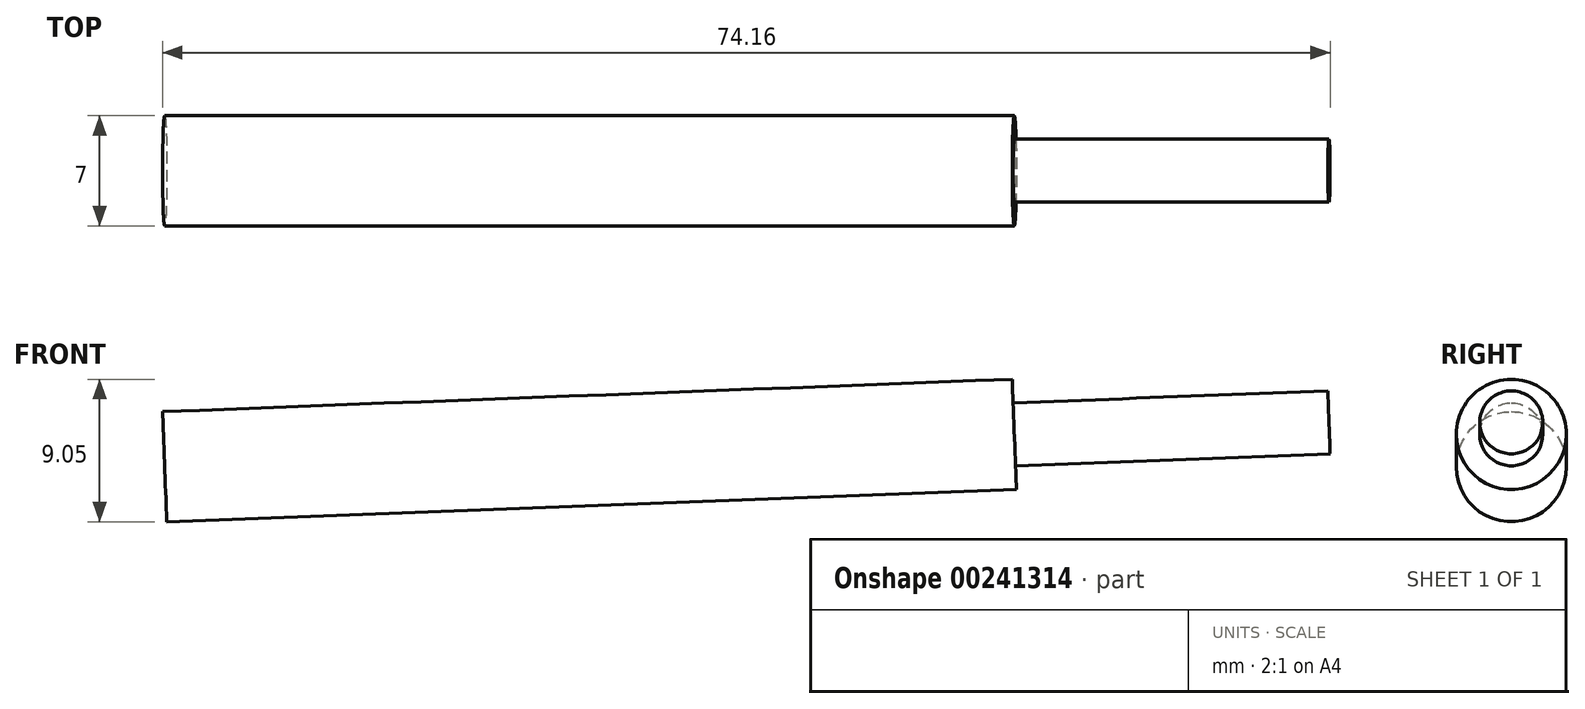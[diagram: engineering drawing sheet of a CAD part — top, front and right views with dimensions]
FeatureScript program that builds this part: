
annotation { "Feature Type Name" : "Feature", "Feature Type Description" : "" }
export const myFeature = defineFeature(function(context is Context, id is Id, definition is map)
    precondition{}
    {
        {
            var Q0;
            Q0=qCreatedBy(makeId("Front.planeOp"),FACE);
            var sketch = newSketch(context, id + "F0", { "sketchPlane" : qUnion([Q0])});
            skLineSegment(sketch, "E0.0", {"start": v(2.14, 3.58) * mm, "end": v(-51.82, 1.53) * mm});
            skLineSegment(sketch, "E1.0", {"start": v(2.2, 2.09) * mm, "end": v(22.18, 2.85) * mm});
            skLineSegment(sketch, "E2", {"start": v(2.2, 2.09) * mm, "end": v(2.14, 3.58) * mm});
            skLineSegment(sketch, "E3", {"start": v(-51.82, 1.53) * mm, "end": v(-51.69, -1.97) * mm});
            skLineSegment(sketch, "E4", {"start": v(22.18, 2.85) * mm, "end": v(22.26, 0.85) * mm});
            skLineSegment(sketch, "E5", {"start": v(-51.69, -1.97) * mm, "end": v(22.26, 0.85) * mm});
            skSolve(sketch);
        }
        {
            var Q0;
            Q0=makeQuery(id+"F0.imprint","IMPRINT",FACE,{"disambiguationData":[TD([[makeQuery(id+"F0.imprint","IMPRINT",EDGE,{"derivedFrom":sQuery(id+"F0.wireOp",EDGE,"E0.0")}),1.0]])]});
            var Q1;
            Q1=sQuery(id+"F0.wireOp",EDGE,"E5");
            revolve(context, id + "F1", {"entities" : qUnion([Q0]), "axis" : qUnion([Q1]), "revolveType" : RevolveType.FULL});
        }
    });
